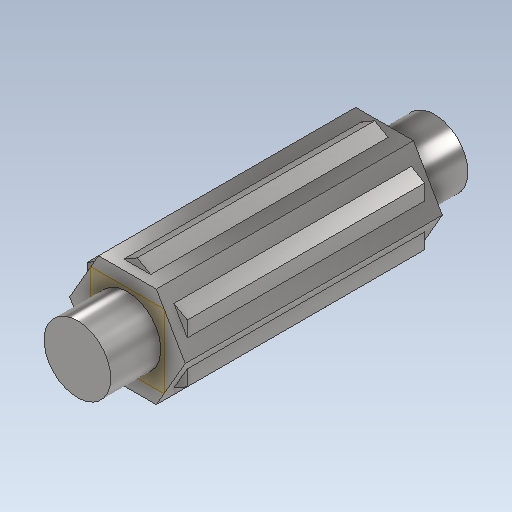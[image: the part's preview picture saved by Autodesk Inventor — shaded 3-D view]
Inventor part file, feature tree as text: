
AUTODESK INVENTOR PART (.ipt)
format: ipt  version: 2023 (Build 270158000, 158)  size: 318,976 bytes
history: native  units: in
note: dims shown in document units (in); Inventor stores cm internally (conversion verified against a paired STEP export)
features: other x3, sketch x2, plane x1, extrude x1
ambient origin geometry x8: Origin, YZ Plane, XZ Plane, XY Plane, X Axis, Y Axis, Z Axis, Center Point
bodies: Solid1 (feature_tree)
feature tree (7):
  other  "CH-1-01-0.25x1.875SmoothShaft.ipt"
  plane  "Work Plane1"
  extrude  "Extrusion1"  [1 undecoded]
  other  "Solid1::CH-1-01-0.25x1.875SmoothShaft.ipt"
  other  "TaggingFeature1"
  sketch  "Sketch1"  dims[d0=0.3937in d1=-0.1875in]
  sketch  "Sketch2"  dims[d2=0.375in d3=0.9636in d4=0.0in]
note: 1 required parameter value undecoded (feature->parameter linkage not recoverable at this tier; creation-order binding heuristic only, values carry confidence <= 0.55)
